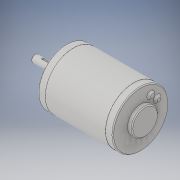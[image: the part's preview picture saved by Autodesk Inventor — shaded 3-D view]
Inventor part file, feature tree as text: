
AUTODESK INVENTOR PART (.ipt)
format: ipt  version: 2018 (Build 220112000, 112)  size: 159,744 bytes
history: native  units: in
note: dims shown in document units (in); Inventor stores cm internally (conversion verified against a paired STEP export)
features: chamfer x1
ambient origin geometry x8: Origin, YZ Plane, XZ Plane, XY Plane, X Axis, Y Axis, Z Axis, Center Point
bodies: Solid1 (feature_tree)
feature tree (1):
  chamfer  "Chamfer3"  [1 undecoded]
note: 1 required parameter value undecoded (feature->parameter linkage not recoverable at this tier; creation-order binding heuristic only, values carry confidence <= 0.55)
